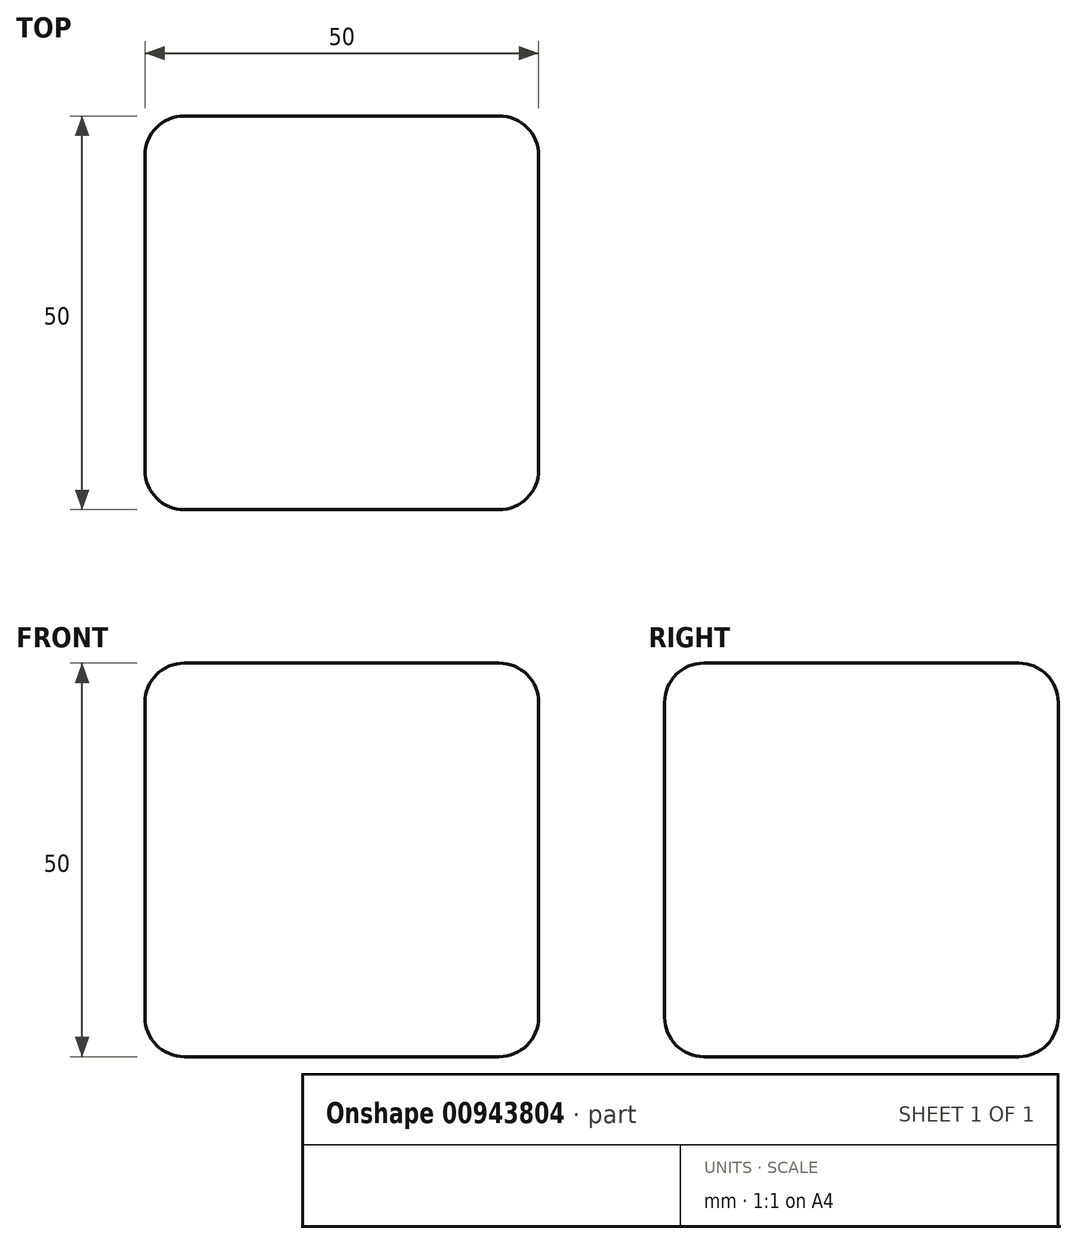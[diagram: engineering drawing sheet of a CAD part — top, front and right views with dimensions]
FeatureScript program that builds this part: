
annotation { "Feature Type Name" : "Feature", "Feature Type Description" : "" }
export const myFeature = defineFeature(function(context is Context, id is Id, definition is map)
    precondition{}
    {
        {
            var Q0;
            Q0=qCreatedBy(makeId("Top.planeOp"),FACE);
            var sketch = newSketch(context, id + "F0", { "sketchPlane" : qUnion([Q0])});
            skLineSegment(sketch, "E0.bottom", {"start": v(0, 0) * mm, "end": v(-50, 0) * mm});
            skLineSegment(sketch, "E0.top", {"start": v(0, -50) * mm, "end": v(-50, -50) * mm});
            skLineSegment(sketch, "E0.left", {"start": v(0, 0) * mm, "end": v(0, -50) * mm});
            skLineSegment(sketch, "E0.right", {"start": v(-50, 0) * mm, "end": v(-50, -50) * mm});
            skSolve(sketch);
        }
        {
            var Q0;
            Q0=makeQuery(id+"F0.imprint","IMPRINT",FACE,{"disambiguationData":[TD([[makeQuery(id+"F0.imprint","IMPRINT",EDGE,{"derivedFrom":sQuery(id+"F0.wireOp",EDGE,"E0.bottom")}),1.0]])]});
            extrude(context, id + "F1", {"entities" : qUnion([Q0]), "depth" : 50 * mm, "offsetDistance" : 25 * mm});
        }
        {
            var Q0;
            Q0=makeQuery(id+"F1.opExtrude","CAP_EDGE",EDGE,{"disambiguationData":[OSD([sQuery(id+"F0.wireOp",EDGE,"E0.left")])],"isStart":false});
            var Q1;
            Q1=makeQuery(id+"F1.opExtrude","CAP_EDGE",EDGE,{"disambiguationData":[OSD([sQuery(id+"F0.wireOp",EDGE,"E0.top")])],"isStart":false});
            var Q2;
            Q2=makeQuery(id+"F1.opExtrude","SWEPT_EDGE",EDGE,{"disambiguationData":[OSD([sQuery(id+"F0.wireOp",EDGE,"E0.top"),sQuery(id+"F0.wireOp",EDGE,"E0.left")])]});
            var Q3;
            Q3=makeQuery(id+"F1.opExtrude","SWEPT_EDGE",EDGE,{"disambiguationData":[OSD([sQuery(id+"F0.wireOp",EDGE,"E0.top"),sQuery(id+"F0.wireOp",EDGE,"E0.right")])]});
            var Q4;
            Q4=makeQuery(id+"F1.opExtrude","CAP_EDGE",EDGE,{"disambiguationData":[OSD([sQuery(id+"F0.wireOp",EDGE,"E0.right")])],"isStart":false});
            var Q5;
            Q5=makeQuery(id+"F1.opExtrude","CAP_EDGE",EDGE,{"disambiguationData":[OSD([sQuery(id+"F0.wireOp",EDGE,"E0.bottom")])],"isStart":false});
            var Q6;
            Q6=makeQuery(id+"F1.opExtrude","SWEPT_EDGE",EDGE,{"disambiguationData":[OSD([sQuery(id+"F0.wireOp",EDGE,"E0.bottom"),sQuery(id+"F0.wireOp",EDGE,"E0.right")])]});
            var Q7;
            Q7=makeQuery(id+"F1.opExtrude","SWEPT_EDGE",EDGE,{"disambiguationData":[OSD([sQuery(id+"F0.wireOp",EDGE,"E0.bottom"),sQuery(id+"F0.wireOp",EDGE,"E0.left")])]});
            var Q8;
            Q8=makeQuery(id+"F1.opExtrude","CAP_EDGE",EDGE,{"disambiguationData":[OSD([sQuery(id+"F0.wireOp",EDGE,"E0.bottom")])],"isStart":true});
            var Q9;
            Q9=makeQuery(id+"F1.opExtrude","CAP_EDGE",EDGE,{"disambiguationData":[OSD([sQuery(id+"F0.wireOp",EDGE,"E0.left")])],"isStart":true});
            var Q10;
            Q10=makeQuery(id+"F1.opExtrude","CAP_EDGE",EDGE,{"disambiguationData":[OSD([sQuery(id+"F0.wireOp",EDGE,"E0.right")])],"isStart":true});
            var Q11;
            Q11=makeQuery(id+"F1.opExtrude","CAP_EDGE",EDGE,{"disambiguationData":[OSD([sQuery(id+"F0.wireOp",EDGE,"E0.top")])],"isStart":true});
            fillet(context, id + "F2", {"entities" : qUnion([Q0, Q1, Q2, Q3, Q4, Q5, Q6, Q7, Q8, Q9, Q10, Q11]), "radius" : 5 * mm, "tangentPropagation" : true, "allowEdgeOverflow" : false});
        }
    });
